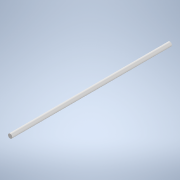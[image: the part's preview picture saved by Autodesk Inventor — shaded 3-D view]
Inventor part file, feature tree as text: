
AUTODESK INVENTOR PART (.ipt)
format: ipt  version: 2022 (Build 260153000, 153)  size: 108,032 bytes
history: native  units: mm
features: other x4, extrude x2, sketch x2, reference x2
ambient origin geometry x8: Origin, YZ Plane, XZ Plane, XY Plane, X Axis, Y Axis, Z Axis, Center Point
bodies: Solid1 (feature_tree)
feature tree (10):
  extrude  "Extrusion1"  Depth=100.0mm TaperAngle=0.0deg
  extrude  "Extrusion2"  Depth=50.0mm TaperAngle=0.0deg
  sketch  "Sketch1"  dims[d0=8.0mm d1=100.0mm d2=0.0mm]
  reference  "Reference1"
  reference  "Reference2"
  sketch  "Sketch2"  dims[d3=3.0mm d4=50.0mm d5=0.0mm]
  other  "<userpath>\OneDrive\Namizje\school\3. letnik\ZOPp\laserski merilnik\3d model\Assembly1.iam"
  other  "Assembly1.iam"
  other  "constraining plate:1"
  other  "Hold of motors:1"
